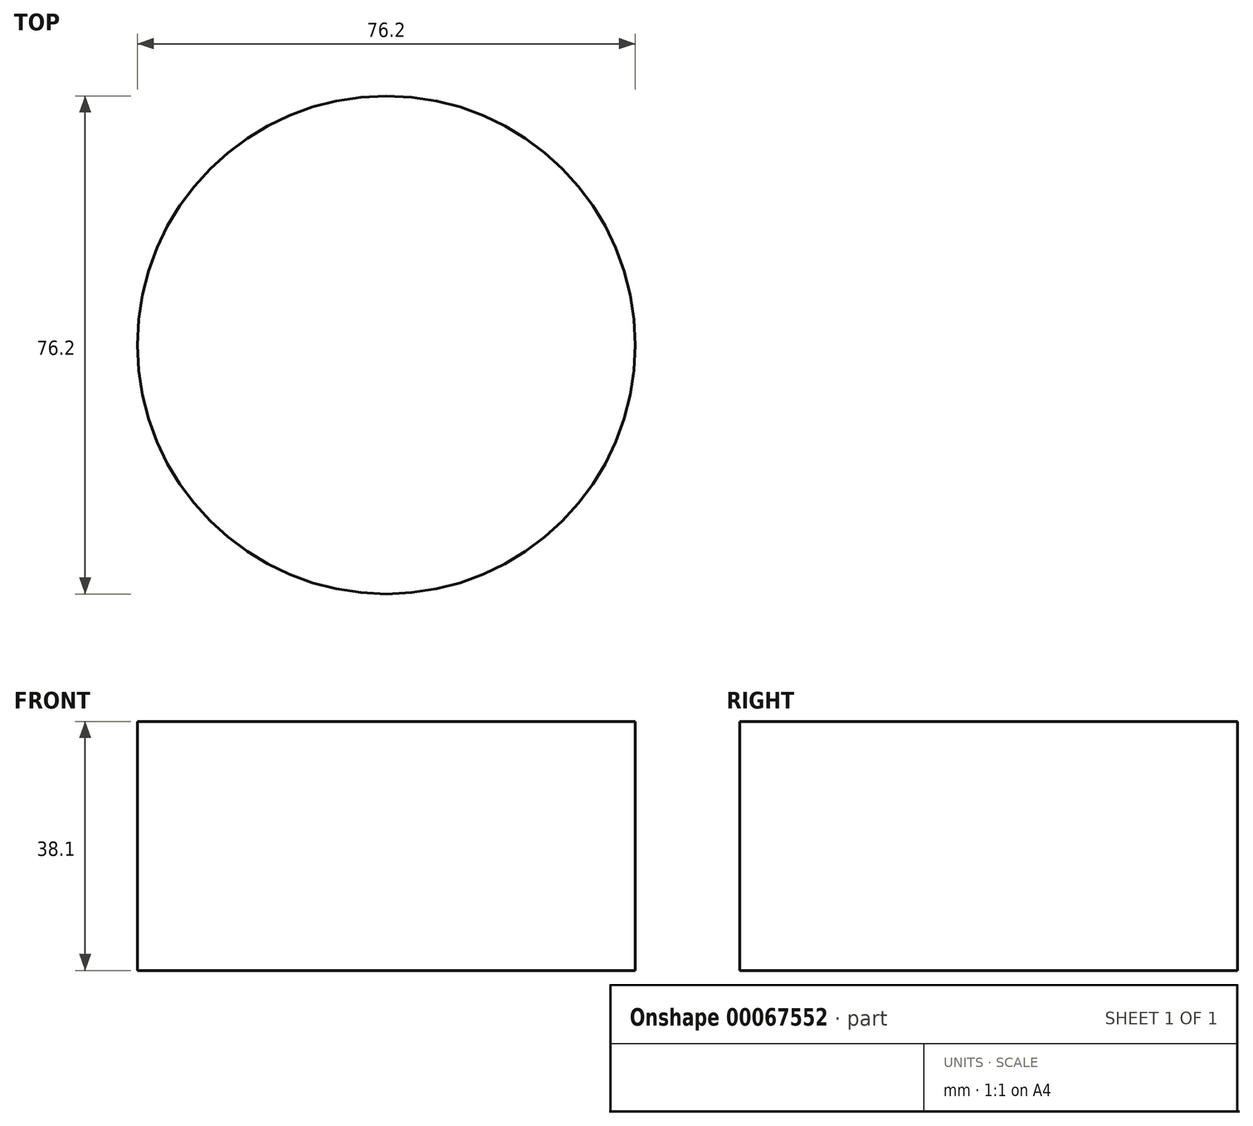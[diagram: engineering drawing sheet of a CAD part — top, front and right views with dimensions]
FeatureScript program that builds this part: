
annotation { "Feature Type Name" : "Feature", "Feature Type Description" : "" }
export const myFeature = defineFeature(function(context is Context, id is Id, definition is map)
    precondition{}
    {
        {
            var Q0;
            Q0=qCreatedBy(makeId("Top.planeOp"),FACE);
            var sketch = newSketch(context, id + "F0", { "sketchPlane" : qUnion([Q0])});
            skCircle(sketch, "E0", {"center": v(0, 0) * mm, "radius": 38.1 * mm});
            skSolve(sketch);
        }
        {
            var Q0;
            Q0=makeQuery(id+"F0.imprint","IMPRINT",FACE,{"disambiguationData":[TD([[makeQuery(id+"F0.imprint","IMPRINT",EDGE,{"derivedFrom":sQuery(id+"F0.wireOp",EDGE,"E0")}),1.0]])]});
            extrude(context, id + "F1", {"entities" : qUnion([Q0]), "endBound" : BoundingType.SYMMETRIC, "depth" : 38.1 * mm});
        }
    });
